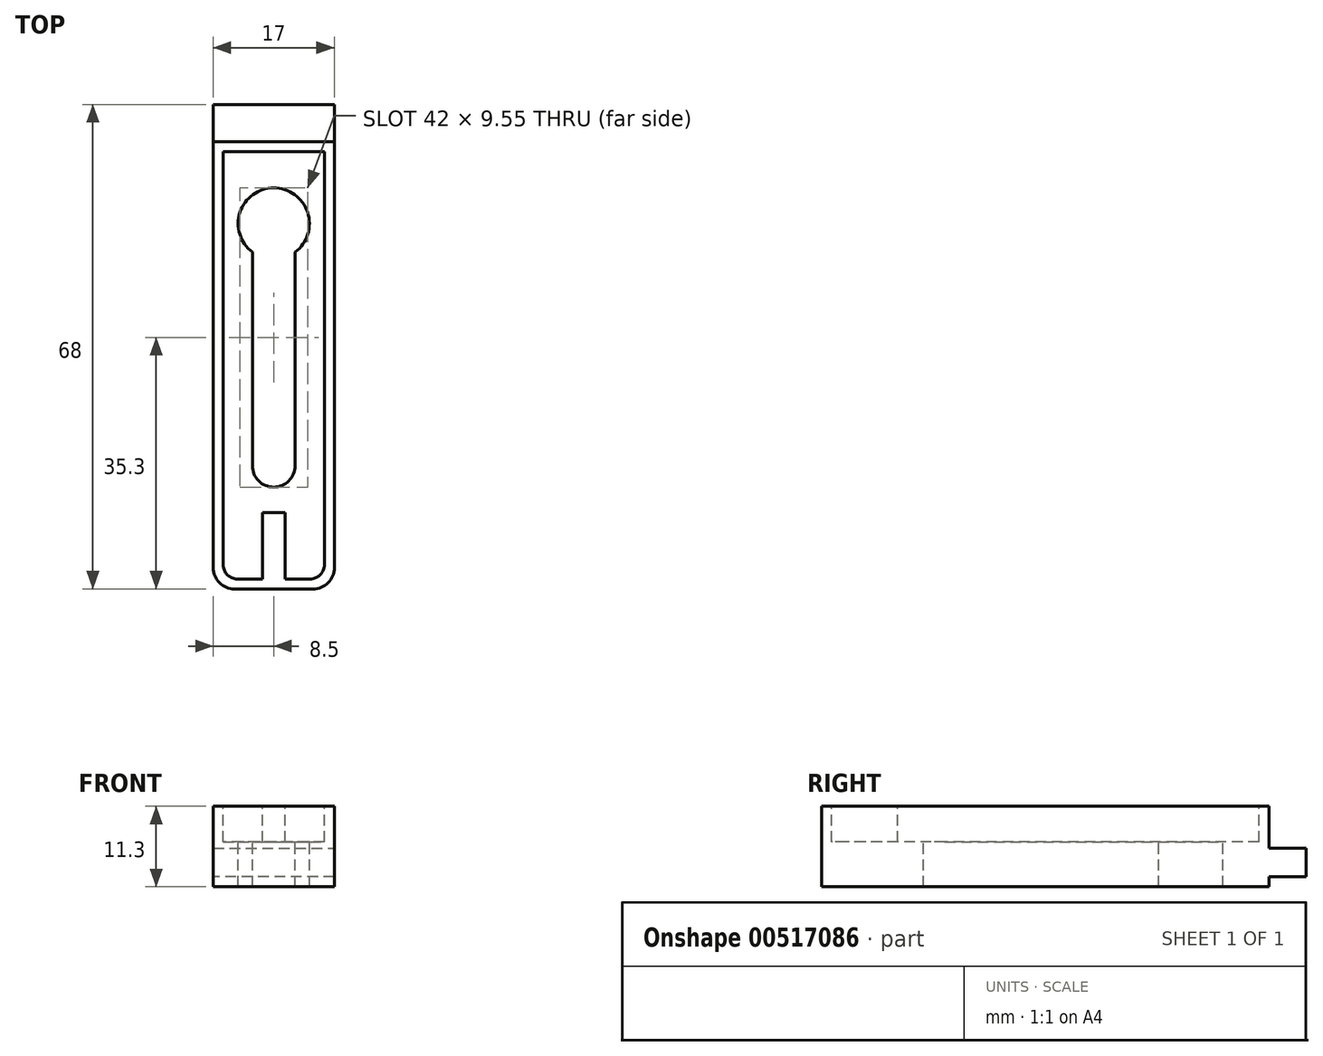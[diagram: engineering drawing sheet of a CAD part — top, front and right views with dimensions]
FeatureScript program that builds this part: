
annotation { "Feature Type Name" : "Feature", "Feature Type Description" : "" }
export const myFeature = defineFeature(function(context is Context, id is Id, definition is map)
    precondition{}
    {
        {
            var Q0;
            Q0=qCreatedBy(makeId("Top.planeOp"),FACE);
            var sketch = newSketch(context, id + "F0", { "sketchPlane" : qUnion([Q0])});
            skLineSegment(sketch, "E0.bottom", {"start": v(8.5, 34) * mm, "end": v(-8.5, 34) * mm});
            skLineSegment(sketch, "E0.top", {"start": v(8.5, -34) * mm, "end": v(-8.5, -34) * mm});
            skLineSegment(sketch, "E0.left", {"start": v(8.5, 34) * mm, "end": v(8.5, -34) * mm});
            skLineSegment(sketch, "E0.right", {"start": v(-8.5, 34) * mm, "end": v(-8.5, -34) * mm});
            skPoint(sketch, "E0.middle", {"position": v(0, 0) * mm});
            skSolve(sketch);
        }
        {
            var Q0;
            Q0=makeQuery(id+"F0.imprint","IMPRINT",FACE,{"disambiguationData":[TD([[makeQuery(id+"F0.imprint","IMPRINT",EDGE,{"derivedFrom":sQuery(id+"F0.wireOp",EDGE,"E0.bottom")}),1.0]])]});
            extrude(context, id + "F1", {"entities" : qUnion([Q0]), "depth" : 11.3 * mm, "offsetDistance" : 25 * mm});
        }
        {
            var Q0;
            Q0=makeQuery(id+"F1.opExtrude","SWEPT_EDGE",EDGE,{"disambiguationData":[OSD([sQuery(id+"F0.wireOp",EDGE,"E0.top"),sQuery(id+"F0.wireOp",EDGE,"E0.left")])]});
            var Q1;
            Q1=makeQuery(id+"F1.opExtrude","SWEPT_EDGE",EDGE,{"disambiguationData":[OSD([sQuery(id+"F0.wireOp",EDGE,"E0.top"),sQuery(id+"F0.wireOp",EDGE,"E0.right")])]});
            fillet(context, id + "F2", {"entities" : qUnion([Q0, Q1]), "radius" : 3 * mm, "tangentPropagation" : true, "allowEdgeOverflow" : false});
        }
        {
            var Q0;
            Q0=makeQuery(id+"F1.opExtrude","CAP_FACE",FACE,{"disambiguationData":[OSD([sQuery(id+"F0.wireOp",EDGE,"E0.bottom"),sQuery(id+"F0.wireOp",EDGE,"E0.top"),sQuery(id+"F0.wireOp",EDGE,"E0.left"),sQuery(id+"F0.wireOp",EDGE,"E0.right")])],"isStart":false});
            var sketch = newSketch(context, id + "F3", { "sketchPlane" : qUnion([Q0])});
            skLineSegment(sketch, "E1.0", {"start": v(-5.1, -32.6) * mm, "end": v(-1.6, -32.6) * mm});
            skLineSegment(sketch, "E1.1", {"start": v(-7.1, 27.4) * mm, "end": v(-7.1, -30.6) * mm});
            skLineSegment(sketch, "E1.3", {"start": v(7.1, -30.6) * mm, "end": v(7.1, 27.4) * mm});
            skLineSegment(sketch, "E2", {"start": v(7.1, 27.4) * mm, "end": v(-7.1, 27.4) * mm});
            skPoint(sketch, "E3.visualSharp", {"position": v(7.1, -32.6) * mm});
            skArc(sketch, "E3.filletArc", {"start": v(5.1, -32.6) * mm, "mid": v(6.51, -32.01) * mm, "end": v(7.1, -30.6) * mm});
            skPoint(sketch, "E4.visualSharp", {"position": v(-7.1, -32.6) * mm});
            skArc(sketch, "E4.filletArc", {"start": v(-7.1, -30.6) * mm, "mid": v(-6.51, -32.01) * mm, "end": v(-5.1, -32.6) * mm});
            skLineSegment(sketch, "E5", {"start": v(0, -32.6) * mm, "end": v(0, -13.12) * mm, "construction": true});
            skPoint(sketch, "E5.endSnap0", {"position": v(0, -32.6) * mm});
            skLineSegment(sketch, "E6.bottom", {"start": v(-1.6, -23.3) * mm, "end": v(1.6, -23.3) * mm});
            skLineSegment(sketch, "E6.left", {"start": v(-1.6, -23.3) * mm, "end": v(-1.6, -32.6) * mm});
            skLineSegment(sketch, "E6.right", {"start": v(1.6, -23.3) * mm, "end": v(1.6, -32.6) * mm});
            skLineSegment(sketch, "E7.trimOffspring", {"start": v(1.6, -32.6) * mm, "end": v(5.1, -32.6) * mm});
            skSolve(sketch);
        }
        {
            var Q0;
            Q0=makeQuery(id+"F3.imprint","IMPRINT",FACE,{"disambiguationData":[TD([[makeQuery(id+"F3.imprint","IMPRINT",EDGE,{"derivedFrom":sQuery(id+"F3.wireOp",EDGE,"E1.0")}),1.0]])]});
            extrude(context, id + "F4", {"entities" : qUnion([Q0]), "operationType" : NewBodyOperationType.REMOVE, "oppositeDirection" : true, "depth" : 5 * mm, "offsetDistance" : 25 * mm});
        }
        {
            var Q0;
            Q0=makeQuery(id+"F4.boolean.opBoolean","COPY",FACE,{"derivedFrom":makeQuery(id+"F4.opExtrude","CAP_FACE",FACE,{"disambiguationData":[OSD([sQuery(id+"F3.wireOp",EDGE,"E1.0"),sQuery(id+"F3.wireOp",EDGE,"E1.1"),sQuery(id+"F3.wireOp",EDGE,"E1.3"),sQuery(id+"F3.wireOp",EDGE,"E2"),sQuery(id+"F3.wireOp",EDGE,"E3.filletArc"),sQuery(id+"F3.wireOp",EDGE,"E4.filletArc"),sQuery(id+"F3.wireOp",EDGE,"E6.bottom"),sQuery(id+"F3.wireOp",EDGE,"E6.left"),sQuery(id+"F3.wireOp",EDGE,"E6.right"),sQuery(id+"F3.wireOp",EDGE,"E7.trimOffspring")])],"isStart":false})});
            var sketch = newSketch(context, id + "F5", { "sketchPlane" : qUnion([Q0])});
            skLineSegment(sketch, "E8.bottom", {"start": v(0, -19.7) * mm, "end": v(0, -19.7) * mm});
            skLineSegment(sketch, "E8.top", {"start": v(0, 20.3) * mm, "end": v(0, 20.3) * mm});
            skLineSegment(sketch, "E8.left", {"start": v(3, -16.7) * mm, "end": v(3, 17.3) * mm});
            skLineSegment(sketch, "E8.right", {"start": v(-3, -16.7) * mm, "end": v(-3, 17.3) * mm});
            skPoint(sketch, "E8.middle", {"position": v(0, 0.3) * mm});
            skPoint(sketch, "E9.visualSharp", {"position": v(-3, 20.3) * mm});
            skArc(sketch, "E9.filletArc", {"start": v(0, 20.3) * mm, "mid": v(-2.12, 19.42) * mm, "end": v(-3, 17.3) * mm});
            skPoint(sketch, "E10.visualSharp", {"position": v(3, 20.3) * mm});
            skArc(sketch, "E10.filletArc", {"start": v(3, 17.3) * mm, "mid": v(2.12, 19.42) * mm, "end": v(0, 20.3) * mm});
            skPoint(sketch, "E11.visualSharp", {"position": v(-3, -19.7) * mm});
            skArc(sketch, "E11.filletArc", {"start": v(-3, -16.7) * mm, "mid": v(-2.12, -18.82) * mm, "end": v(0, -19.7) * mm});
            skPoint(sketch, "E12.visualSharp", {"position": v(3, -19.7) * mm});
            skArc(sketch, "E12.filletArc", {"start": v(0, -19.7) * mm, "mid": v(2.12, -18.82) * mm, "end": v(3, -16.7) * mm});
            skSolve(sketch);
        }
        {
            var Q0;
            Q0 = qSketchRegion(id + "F5", true);
            extrude(context, id + "F6", {"entities" : qUnion([Q0]), "operationType" : NewBodyOperationType.REMOVE, "oppositeDirection" : true, "depth" : 25 * mm, "offsetDistance" : 25 * mm});
        }
        {
            var Q0;
            Q0=makeQuery(id+"F1.opExtrude","SWEPT_FACE",FACE,{"disambiguationData":[OSD([sQuery(id+"F0.wireOp",EDGE,"E0.left")])]});
            var sketch = newSketch(context, id + "F7", { "sketchPlane" : qUnion([Q0])});
            skLineSegment(sketch, "E13.bottom", {"start": v(28.8, 13.67) * mm, "end": v(38.97, 13.67) * mm});
            skLineSegment(sketch, "E13.top", {"start": v(28.8, 5.4) * mm, "end": v(38.97, 5.4) * mm});
            skLineSegment(sketch, "E13.left", {"start": v(28.8, 13.67) * mm, "end": v(28.8, 5.4) * mm});
            skLineSegment(sketch, "E13.right", {"start": v(38.97, 13.67) * mm, "end": v(38.97, 5.4) * mm});
            skLineSegment(sketch, "E14.bottom", {"start": v(38.97, 1.4) * mm, "end": v(28.8, 1.4) * mm});
            skLineSegment(sketch, "E14.top", {"start": v(38.97, -3.97) * mm, "end": v(28.8, -3.97) * mm});
            skLineSegment(sketch, "E14.left", {"start": v(38.97, 1.4) * mm, "end": v(38.97, -3.97) * mm});
            skLineSegment(sketch, "E14.right", {"start": v(28.8, 1.4) * mm, "end": v(28.8, -3.97) * mm});
            skSolve(sketch);
        }
        {
            var Q0;
            Q0 = qSketchRegion(id + "F7", true);
            extrude(context, id + "F8", {"entities" : qUnion([Q0]), "operationType" : NewBodyOperationType.REMOVE, "oppositeDirection" : true, "depth" : 25 * mm, "offsetDistance" : 25 * mm});
        }
        {
            var Q0;
            Q0=makeQuery(id+"F4.boolean.opBoolean","COPY",FACE,{"derivedFrom":makeQuery(id+"F4.opExtrude","CAP_FACE",FACE,{"disambiguationData":[OSD([sQuery(id+"F3.wireOp",EDGE,"E1.0"),sQuery(id+"F3.wireOp",EDGE,"E1.1"),sQuery(id+"F3.wireOp",EDGE,"E1.3"),sQuery(id+"F3.wireOp",EDGE,"E2"),sQuery(id+"F3.wireOp",EDGE,"E3.filletArc"),sQuery(id+"F3.wireOp",EDGE,"E4.filletArc"),sQuery(id+"F3.wireOp",EDGE,"E6.bottom"),sQuery(id+"F3.wireOp",EDGE,"E6.left"),sQuery(id+"F3.wireOp",EDGE,"E6.right"),sQuery(id+"F3.wireOp",EDGE,"E7.trimOffspring")])],"isStart":false})});
            var sketch = newSketch(context, id + "F9", { "sketchPlane" : qUnion([Q0])});
            skCircle(sketch, "E15", {"center": v(0, 17.3) * mm, "radius": 5 * mm});
            skSolve(sketch);
        }
        {
            var Q0;
            Q0 = qSketchRegion(id + "F9", true);
            extrude(context, id + "F10", {"entities" : qUnion([Q0]), "operationType" : NewBodyOperationType.REMOVE, "oppositeDirection" : true, "depth" : 25 * mm, "offsetDistance" : 25 * mm});
        }
    });
